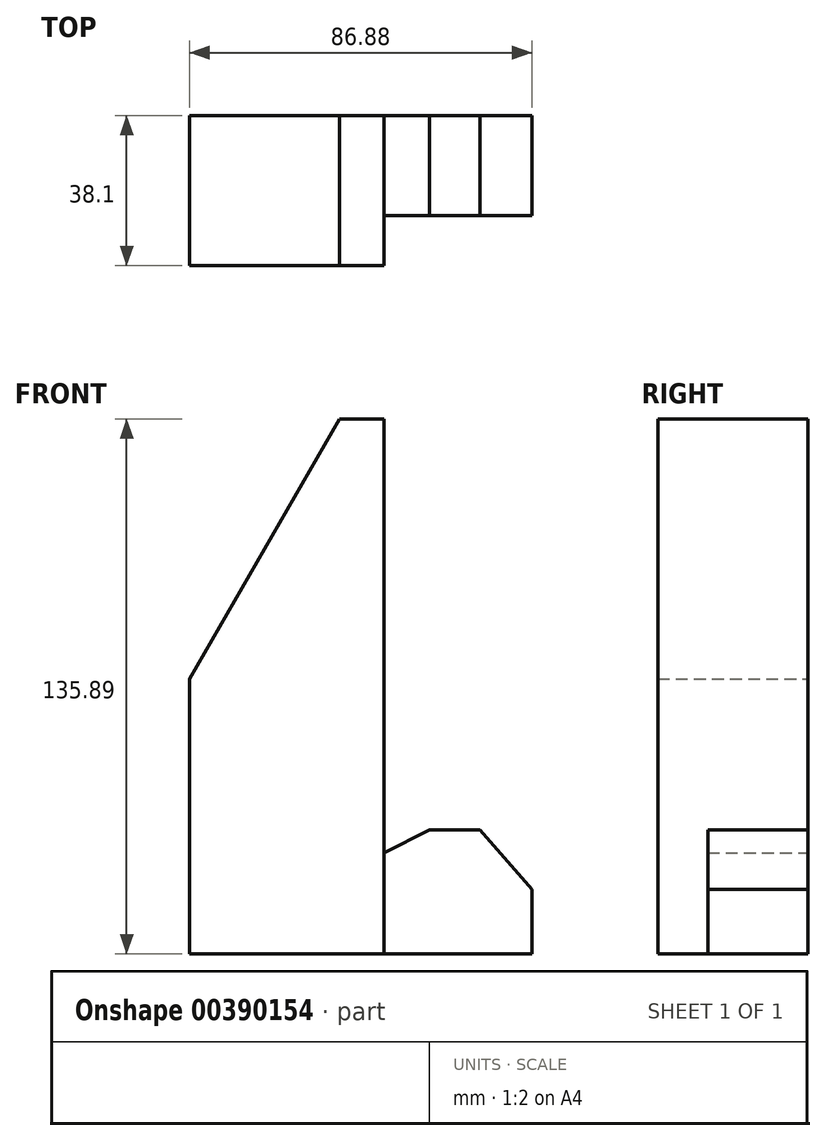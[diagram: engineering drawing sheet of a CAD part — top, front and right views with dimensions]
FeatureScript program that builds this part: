
annotation { "Feature Type Name" : "Feature", "Feature Type Description" : "" }
export const myFeature = defineFeature(function(context is Context, id is Id, definition is map)
    precondition{}
    {
        {
            var Q0;
            Q0=qCreatedBy(makeId("Front.planeOp"),FACE);
            var sketch = newSketch(context, id + "F0", { "sketchPlane" : qUnion([Q0])});
            skLineSegment(sketch, "E0", {"start": v(-175.06, 0) * mm, "end": v(-175.06, 19.05) * mm});
            skLineSegment(sketch, "E1", {"start": v(-175.06, 19.05) * mm, "end": v(-150.2, 31.48) * mm});
            skLineSegment(sketch, "E2", {"start": v(-150.2, 31.48) * mm, "end": v(-137.42, 31.48) * mm});
            skLineSegment(sketch, "E3", {"start": v(-137.42, 31.48) * mm, "end": v(-124.26, 16.45) * mm});
            skLineSegment(sketch, "E4", {"start": v(-124.26, 16.45) * mm, "end": v(-124.26, 0) * mm});
            skLineSegment(sketch, "E5", {"start": v(-124.26, 0) * mm, "end": v(-175.06, 0) * mm});
            skSolve(sketch);
        }
        {
            var Q0;
            Q0=makeQuery(id+"F0.imprint","IMPRINT",FACE,{"disambiguationData":[TD([[makeQuery(id+"F0.imprint","IMPRINT",EDGE,{"derivedFrom":sQuery(id+"F0.wireOp",EDGE,"E0")}),-1.0]])]});
            extrude(context, id + "F1", {"entities" : qUnion([Q0]), "depth" : 25.4 * mm});
        }
        {
            var Q0;
            Q0=qCreatedBy(makeId("Front.planeOp"),FACE);
            var sketch = newSketch(context, id + "F2", { "sketchPlane" : qUnion([Q0])});
            skLineSegment(sketch, "E6", {"start": v(-211.14, 0) * mm, "end": v(-211.14, 69.85) * mm});
            skLineSegment(sketch, "E7", {"start": v(-211.14, 69.85) * mm, "end": v(-173.13, 135.9) * mm});
            skLineSegment(sketch, "E8", {"start": v(-173.13, 135.9) * mm, "end": v(-161.73, 135.9) * mm});
            skLineSegment(sketch, "E9", {"start": v(-161.73, 135.9) * mm, "end": v(-161.73, 0) * mm});
            skLineSegment(sketch, "E10", {"start": v(-161.73, 0) * mm, "end": v(-211.14, 0) * mm});
            skSolve(sketch);
        }
        {
            var Q0;
            Q0=makeQuery(id+"F2.imprint","IMPRINT",FACE,{"disambiguationData":[TD([[makeQuery(id+"F2.imprint","IMPRINT",EDGE,{"derivedFrom":sQuery(id+"F2.wireOp",EDGE,"E6")}),-1.0]])]});
            extrude(context, id + "F3", {"entities" : qUnion([Q0]), "operationType" : NewBodyOperationType.ADD, "depth" : 38.1 * mm});
        }
    });
